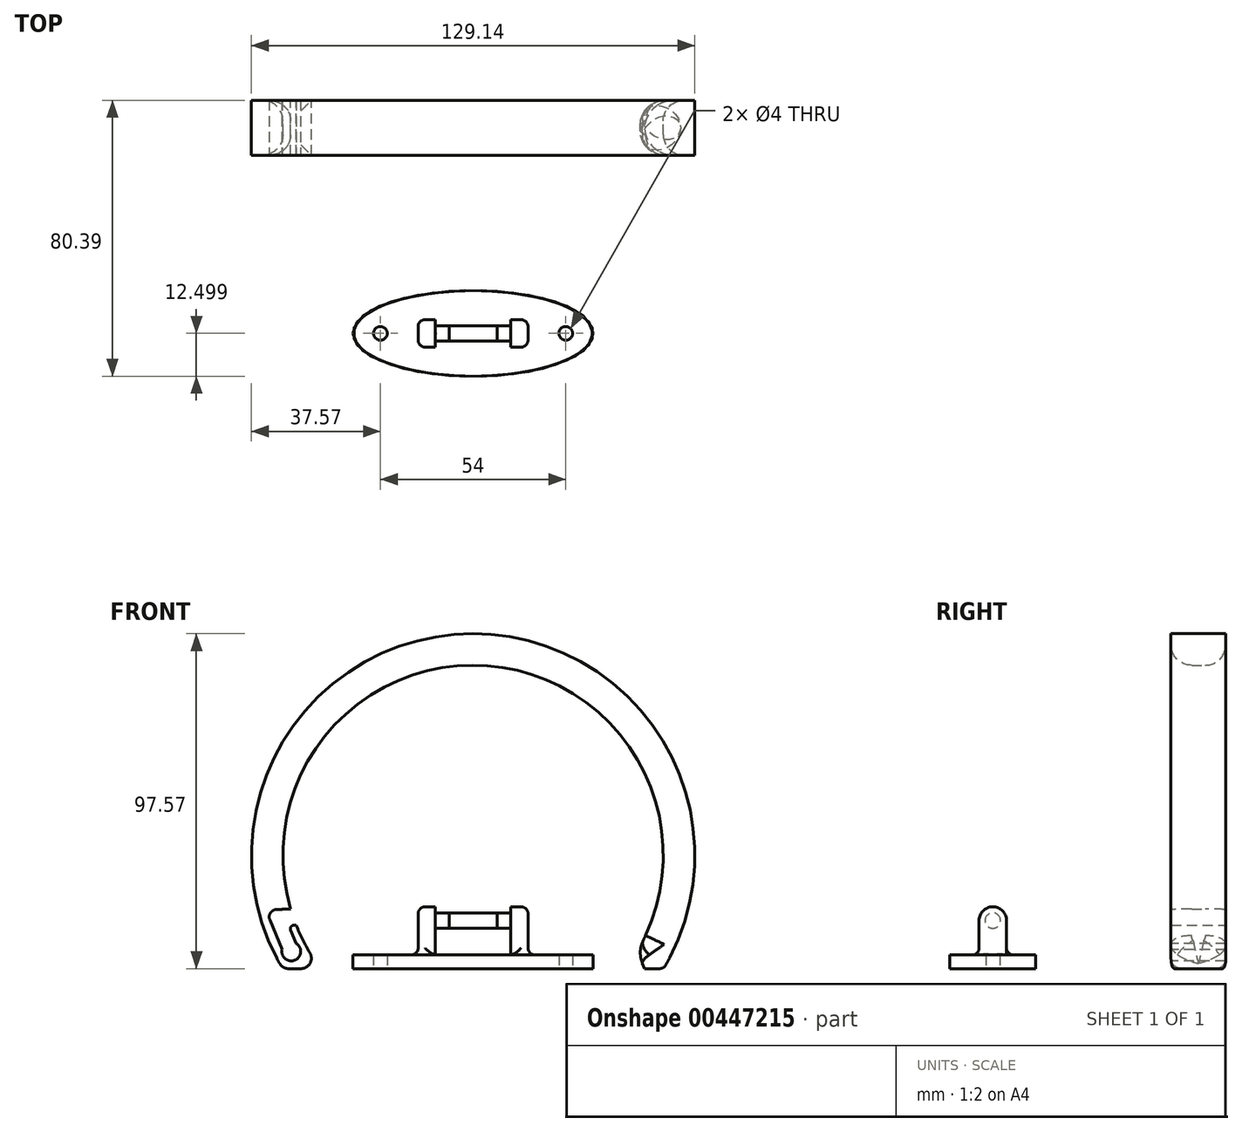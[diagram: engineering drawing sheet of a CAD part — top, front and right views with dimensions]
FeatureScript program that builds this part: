
annotation { "Feature Type Name" : "Feature", "Feature Type Description" : "" }
export const myFeature = defineFeature(function(context is Context, id is Id, definition is map)
    precondition{}
    {
        {
            var Q0;
            Q0=qCreatedBy(makeId("Front.planeOp"),FACE);
            var sketch = newSketch(context, id + "F0", { "sketchPlane" : qUnion([Q0])});
            skArc(sketch, "E0", {"start": v(50, 0) * mm, "mid": v(0, 92.9) * mm, "end": v(-50, 0) * mm});
            skArc(sketch, "E1", {"start": v(50, 0) * mm, "mid": v(41.45, -2.98) * mm, "end": v(36.33, 4.49) * mm});
            skSolve(sketch);
        }
        {
            var Q0;
            Q0=qCreatedBy(makeId("Top.planeOp"),FACE);
            var sketch = newSketch(context, id + "F1", { "sketchPlane" : qUnion([Q0])});
            skLineSegment(sketch, "E2.bottom", {"start": v(-44.5, 8) * mm, "end": v(-55.5, 8) * mm});
            skLineSegment(sketch, "E2.top", {"start": v(-44.5, -8) * mm, "end": v(-55.5, -8) * mm});
            skLineSegment(sketch, "E2.left", {"start": v(-44.5, 8) * mm, "end": v(-44.5, -8) * mm});
            skLineSegment(sketch, "E2.right", {"start": v(-55.5, 8) * mm, "end": v(-55.5, -8) * mm});
            skPoint(sketch, "E2.middle", {"position": v(-50, 0) * mm});
            skSolve(sketch);
        }
        {
            var Q0;
            Q0=makeQuery(id+"F1.imprint","IMPRINT",FACE,{"disambiguationData":[TD([[makeQuery(id+"F1.imprint","IMPRINT",EDGE,{"derivedFrom":sQuery(id+"F1.wireOp",EDGE,"E2.bottom")}),1.0]])]});
            var Q1;
            Q1=sQuery(id+"F0.wireOp",EDGE,"E0");
            sweep(context, id + "F2", {"profiles" : qUnion([Q0]), "path" : qUnion([Q1])});
        }
        {
            var Q0;
            Q0=makeQuery(id+"F2.opSweep","CAP_EDGE",EDGE,{"disambiguationData":[OSD([sQuery(id+"F0.wireOp",VERTEX,"E0.end"),sQuery(id+"F1.wireOp",EDGE,"ZPRCqQeq-nia5-ead6-5WME-yqNuvtyTv4r0")])],"isStart":true});
            fillet(context, id + "F3", {"entities" : qUnion([Q0]), "radius" : 3 * mm, "tangentPropagation" : true, "allowEdgeOverflow" : false});
        }
        {
            var Q0;
            Q0=qCreatedBy(makeId("Front.planeOp"),FACE);
            var sketch = newSketch(context, id + "F4", { "sketchPlane" : qUnion([Q0])});
            skPoint(sketch, "E3", {"position": v(-52.96, 5) * mm});
            skPoint(sketch, "E4", {"position": v(-57.14, 15) * mm});
            skPoint(sketch, "E5", {"position": v(-47.14, 15) * mm});
            skCircle(sketch, "E6", {"center": v(-47.14, 15) * mm, "radius": 2.5 * mm});
            skCircle(sketch, "E7", {"center": v(-57.14, 15) * mm, "radius": 2.25 * mm});
            skCircle(sketch, "E8", {"center": v(-52.96, 5) * mm, "radius": 2.25 * mm});
            skLineSegment(sketch, "E9", {"start": v(-50.89, 5.87) * mm, "end": v(-55.06, 15.87) * mm});
            skLineSegment(sketch, "E10", {"start": v(-55.04, 4.13) * mm, "end": v(-59.22, 14.13) * mm});
            skLineSegment(sketch, "E11", {"start": v(-47.2, 17.5) * mm, "end": v(-57.2, 17.25) * mm});
            skLineSegment(sketch, "E12", {"start": v(-47.2, 12.5) * mm, "end": v(-57.2, 12.75) * mm});
            skCircle(sketch, "E13", {"center": v(-52.96, 5) * mm, "radius": 2.75 * mm});
            skSolve(sketch);
        }
        {
            var Q0;
            {var subQ0=sQuery(id+"F4.wireOp",EDGE,"E6");var subQ1=makeQuery(id+"F4.imprint","INTERSECT",VERTEX,{"derivedFrom":[subQ0,sQuery(id+"F4.wireOp",EDGE,"E11")]});Q0=makeQuery(id+"F4.imprint","IMPRINT",FACE,{"disambiguationData":[TD([[makeQuery(id+"F4.imprint","IMPRINT",EDGE,{"disambiguationData":[TD([[subQ1,-1.0]])],"derivedFrom":subQ0}),1.0]])]});}
            var Q1;
            {var subQ0=sQuery(id+"F4.wireOp",EDGE,"E11");Q1=makeQuery(id+"F4.imprint","IMPRINT",FACE,{"disambiguationData":[TD([[makeQuery(id+"F4.imprint","IMPRINT",EDGE,{"derivedFrom":subQ0}),1.0]])]});}
            var Q2;
            {var subQ0=sQuery(id+"F4.wireOp",EDGE,"E7");var subQ1=makeQuery(id+"F4.imprint","INTERSECT",VERTEX,{"derivedFrom":[subQ0,sQuery(id+"F4.wireOp",EDGE,"E9")]});Q2=makeQuery(id+"F4.imprint","IMPRINT",FACE,{"disambiguationData":[TD([[makeQuery(id+"F4.imprint","IMPRINT",EDGE,{"disambiguationData":[TD([[subQ1,-1.0]])],"derivedFrom":subQ0}),1.0]])]});}
            var Q3;
            {var subQ1=sQuery(id+"F4.wireOp",EDGE,"E7");var subQ5=sQuery(id+"F4.wireOp",EDGE,"E10");var subQ6=makeQuery(id+"F4.imprint","INTERSECT",VERTEX,{"derivedFrom":[subQ1,subQ5]});Q3=makeQuery(id+"F4.imprint","IMPRINT",FACE,{"disambiguationData":[TD([[makeQuery(id+"F4.imprint","IMPRINT",EDGE,{"disambiguationData":[TD([[subQ6,-1.0]])],"derivedFrom":subQ1}),-1.0]])]});}
            var Q4;
            {var subQ0=sQuery(id+"F4.wireOp",EDGE,"E9");var subQ1=sQuery(id+"F4.wireOp",EDGE,"E7");var subQ2=makeQuery(id+"F4.imprint","INTERSECT",VERTEX,{"derivedFrom":[subQ1,subQ0]});Q4=makeQuery(id+"F4.imprint","IMPRINT",FACE,{"disambiguationData":[TD([[makeQuery(id+"F4.imprint","IMPRINT",EDGE,{"disambiguationData":[TD([[subQ2,1.0]])],"derivedFrom":subQ1}),-1.0]])]});}
            var Q5;
            {var subQ0=sQuery(id+"F4.wireOp",EDGE,"E9");var subQ1=sQuery(id+"F4.wireOp",EDGE,"E8");var subQ2=makeQuery(id+"F4.imprint","INTERSECT",VERTEX,{"derivedFrom":[subQ1,subQ0]});Q5=makeQuery(id+"F4.imprint","IMPRINT",FACE,{"disambiguationData":[TD([[makeQuery(id+"F4.imprint","IMPRINT",EDGE,{"disambiguationData":[TD([[subQ2,-1.0]])],"derivedFrom":subQ1}),-1.0]])]});}
            var Q6;
            {var subQ0=sQuery(id+"F4.wireOp",EDGE,"E9");var subQ1=sQuery(id+"F4.wireOp",EDGE,"E8");var subQ2=makeQuery(id+"F4.imprint","INTERSECT",VERTEX,{"derivedFrom":[subQ1,subQ0]});Q6=makeQuery(id+"F4.imprint","IMPRINT",FACE,{"disambiguationData":[TD([[makeQuery(id+"F4.imprint","IMPRINT",EDGE,{"disambiguationData":[TD([[subQ2,1.0]])],"derivedFrom":subQ1}),-1.0]])]});}
            var Q7;
            {var subQ0=sQuery(id+"F4.wireOp",EDGE,"E8");var subQ1=makeQuery(id+"F4.imprint","INTERSECT",VERTEX,{"derivedFrom":[subQ0,sQuery(id+"F4.wireOp",EDGE,"E9")]});Q7=makeQuery(id+"F4.imprint","IMPRINT",FACE,{"disambiguationData":[TD([[makeQuery(id+"F4.imprint","IMPRINT",EDGE,{"disambiguationData":[TD([[subQ1,-1.0]])],"derivedFrom":subQ0}),1.0]])]});}
            extrude(context, id + "F5", {"entities" : qUnion([Q0, Q1, Q2, Q3, Q4, Q5, Q6, Q7]), "operationType" : NewBodyOperationType.REMOVE, "oppositeDirection" : true, "depth" : 12 * mm, "hasSecondDirection" : true, "secondDirectionOppositeDirection" : false, "secondDirectionDepth" : 12 * mm, "offsetDistance" : 25 * mm});
        }
        {
            var Q0;
            Q0=makeQuery(id+"F5.boolean.opBoolean","COPY",EDGE,{"derivedFrom":makeQuery(id+"F5.opExtrude","SWEPT_EDGE",EDGE,{"disambiguationData":[OSD([sQuery(id+"F4.wireOp",EDGE,"E9"),sQuery(id+"F4.wireOp",EDGE,"E12")])]})});
            fillet(context, id + "F6", {"entities" : qUnion([Q0]), "radius" : 1 * mm, "tangentPropagation" : true, "allowEdgeOverflow" : false});
        }
        {
            var Q0;
            {var subQ0=sQuery(id+"F1.wireOp",EDGE,"E2.left");var subQ1=sQuery(id+"F1.wireOp",EDGE,"E2.bottom");var subQ2=sQuery(id+"F0.wireOp",EDGE,"E0");Q0=makeQuery(id+"F5.boolean.opBoolean","SPLIT",EDGE,{"disambiguationData":[TD([makeQuery(id+"F5.opExtrude","SWEPT_FACE",FACE,{"disambiguationData":[OSD([sQuery(id+"F4.wireOp",EDGE,"E11")])]})])],"derivedFrom":makeQuery(id+"F2.opSweep","SWEPT_EDGE",EDGE,{"disambiguationData":[OSD([subQ2,subQ1,subQ0])]})});}
            var Q1;
            {var subQ0=sQuery(id+"F1.wireOp",EDGE,"E2.left");var subQ1=sQuery(id+"F1.wireOp",EDGE,"E2.top");var subQ2=sQuery(id+"F0.wireOp",EDGE,"E0");Q1=makeQuery(id+"F5.boolean.opBoolean","SPLIT",EDGE,{"disambiguationData":[TD([makeQuery(id+"F5.opExtrude","SWEPT_FACE",FACE,{"disambiguationData":[OSD([sQuery(id+"F4.wireOp",EDGE,"E11")])]})])],"derivedFrom":makeQuery(id+"F2.opSweep","SWEPT_EDGE",EDGE,{"disambiguationData":[OSD([subQ2,subQ1,subQ0])]})});}
            fillet(context, id + "F7", {"entities" : qUnion([Q0, Q1]), "radius" : 6 * mm, "tangentPropagation" : true, "allowEdgeOverflow" : false});
        }
        {
            var Q0;
            Q0=makeQuery(id+"F2.opSweep","CAP_EDGE",EDGE,{"disambiguationData":[OSD([sQuery(id+"F0.wireOp",VERTEX,"E0.start"),sQuery(id+"F1.wireOp",EDGE,"E2.left")])],"isStart":false});
            fillet(context, id + "F8", {"entities" : qUnion([Q0]), "radius" : 8 * mm, "tangentPropagation" : true, "allowEdgeOverflow" : false});
        }
        {
            var Q0;
            Q0=qCreatedBy(makeId("Top.planeOp"),FACE);
            var sketch = newSketch(context, id + "F9", { "sketchPlane" : qUnion([Q0])});
            skLineSegment(sketch, "E14.bottom", {"start": v(68.74, 41) * mm, "end": v(27.5, 41) * mm});
            skLineSegment(sketch, "E14.top", {"start": v(68.74, -30.42) * mm, "end": v(27.5, -30.42) * mm});
            skLineSegment(sketch, "E14.left", {"start": v(68.74, 41) * mm, "end": v(68.74, -30.42) * mm});
            skLineSegment(sketch, "E14.right", {"start": v(27.5, 41) * mm, "end": v(27.5, -30.42) * mm});
            skSolve(sketch);
        }
        {
            var Q0;
            Q0=makeQuery(id+"F9.imprint","IMPRINT",FACE,{"disambiguationData":[TD([[makeQuery(id+"F9.imprint","IMPRINT",EDGE,{"derivedFrom":sQuery(id+"F9.wireOp",EDGE,"E14.bottom")}),1.0]])]});
            extrude(context, id + "F10", {"entities" : qUnion([Q0]), "operationType" : NewBodyOperationType.REMOVE, "oppositeDirection" : true, "depth" : 25 * mm});
        }
        {
            var Q0;
            Q0=makeQuery(id+"F10.boolean.opBoolean","INTERSECT",EDGE,{"derivedFrom":[makeQuery(id+"F2.opSweep","SWEPT_FACE",FACE,{"disambiguationData":[OSD([sQuery(id+"F0.wireOp",EDGE,"E0"),sQuery(id+"F1.wireOp",EDGE,"E2.right")])]}),makeQuery(id+"F10.opExtrude","CAP_FACE",FACE,{"disambiguationData":[OSD([sQuery(id+"F9.wireOp",EDGE,"E14.bottom"),sQuery(id+"F9.wireOp",EDGE,"E14.top"),sQuery(id+"F9.wireOp",EDGE,"E14.left"),sQuery(id+"F9.wireOp",EDGE,"E14.right")])],"isStart":true})]});
            var Q1;
            Q1=makeQuery(id+"F10.boolean.opBoolean","INTERSECT",EDGE,{"derivedFrom":[makeQuery(id+"F2.opSweep","CAP_FACE",FACE,{"disambiguationData":[OSD([sQuery(id+"F0.wireOp",VERTEX,"E0.start"),sQuery(id+"F1.wireOp",EDGE,"E2.bottom"),sQuery(id+"F1.wireOp",EDGE,"E2.top"),sQuery(id+"F1.wireOp",EDGE,"E2.left"),sQuery(id+"F1.wireOp",EDGE,"E2.right")])],"isStart":false}),makeQuery(id+"F10.opExtrude","CAP_FACE",FACE,{"disambiguationData":[OSD([sQuery(id+"F9.wireOp",EDGE,"E14.bottom"),sQuery(id+"F9.wireOp",EDGE,"E14.top"),sQuery(id+"F9.wireOp",EDGE,"E14.left"),sQuery(id+"F9.wireOp",EDGE,"E14.right")])],"isStart":true})]});
            fillet(context, id + "F11", {"entities" : qUnion([Q0, Q1]), "radius" : 2 * mm, "tangentPropagation" : true, "allowEdgeOverflow" : false});
        }
        {
            var Q0;
            Q0=qCreatedBy(makeId("Top.planeOp"),FACE);
            var sketch = newSketch(context, id + "F12", { "sketchPlane" : qUnion([Q0])});
            skEllipse(sketch, "E15", {"center": v(0, -59.9) * mm, "majorRadius": 35 * mm, "minorRadius": 12.5 * mm, "majorAxis": v(1, 0)});
            skPoint(sketch, "E16", {"position": v(27, -59.9) * mm});
            skPoint(sketch, "E17", {"position": v(-27, -59.9) * mm});
            skSolve(sketch);
        }
        {
            var Q0;
            Q0=makeQuery(id+"F12.imprint","IMPRINT",FACE,{"disambiguationData":[TD([[makeQuery(id+"F12.imprint","IMPRINT",EDGE,{"derivedFrom":sQuery(id+"F12.wireOp",EDGE,"E15")}),1.0]])]});
            extrude(context, id + "F13", {"entities" : qUnion([Q0]), "depth" : 4 * mm});
        }
        {
            var Q0;
            Q0=qCreatedBy(makeId("Right.planeOp"),FACE);
            cPlane(context, id + "F14", {"entities" : qUnion([Q0]), "cplaneType" : CPlaneType.OFFSET, "offset" : 11 * mm, "width" : 150 * mm, "height" : 150 * mm});
        }
        {
            var Q0;
            Q0=qCreatedBy(id+"F14.planeOp",FACE);
            var sketch = newSketch(context, id + "F15", { "sketchPlane" : qUnion([Q0])});
            skLineSegment(sketch, "E18.bottom", {"start": v(-63.9, 0) * mm, "end": v(-55.9, 0) * mm});
            skLineSegment(sketch, "E18.top", {"start": v(-63.9, 18) * mm, "end": v(-55.9, 18) * mm});
            skLineSegment(sketch, "E18.left", {"start": v(-63.9, 0) * mm, "end": v(-63.9, 18) * mm});
            skLineSegment(sketch, "E18.right", {"start": v(-55.9, 0) * mm, "end": v(-55.9, 18) * mm});
            skCircle(sketch, "E19", {"center": v(-59.9, 14) * mm, "radius": 2.25 * mm});
            skSolve(sketch);
        }
        {
            var Q0;
            Q0=makeQuery(id+"F15.imprint","IMPRINT",FACE,{"disambiguationData":[TD([[makeQuery(id+"F15.imprint","IMPRINT",EDGE,{"derivedFrom":sQuery(id+"F15.wireOp",EDGE,"E18.bottom")}),1.0]])]});
            var Q1;
            Q1=makeQuery(id+"F15.imprint","IMPRINT",FACE,{"disambiguationData":[TD([[makeQuery(id+"F15.imprint","IMPRINT",EDGE,{"derivedFrom":sQuery(id+"F15.wireOp",EDGE,"E19")}),1.0]])]});
            extrude(context, id + "F16", {"entities" : qUnion([Q0, Q1]), "operationType" : NewBodyOperationType.ADD, "depth" : 5 * mm});
        }
        {
            var Q0;
            Q0=makeQuery(id+"F15.imprint","IMPRINT",FACE,{"disambiguationData":[TD([[makeQuery(id+"F15.imprint","IMPRINT",EDGE,{"derivedFrom":sQuery(id+"F15.wireOp",EDGE,"E19")}),1.0]])]});
            var Q1;
            Q1=sQuery(id+"F15.wireOp",EDGE,"E19");
            extrude(context, id + "F17", {"entities" : qUnion([Q0]), "operationType" : NewBodyOperationType.ADD, "surfaceEntities" : qUnion([Q1]), "oppositeDirection" : true, "depth" : 18 * mm});
        }
        {
            var Q0;
            Q0=makeQuery(id+"F16.opExtrude","SWEPT_EDGE",EDGE,{"disambiguationData":[OSD([sQuery(id+"F15.wireOp",EDGE,"E18.top"),sQuery(id+"F15.wireOp",EDGE,"E18.left")])]});
            var Q1;
            Q1=makeQuery(id+"F16.opExtrude","SWEPT_EDGE",EDGE,{"disambiguationData":[OSD([sQuery(id+"F15.wireOp",EDGE,"E18.top"),sQuery(id+"F15.wireOp",EDGE,"E18.right")])]});
            fillet(context, id + "F18", {"entities" : qUnion([Q0, Q1]), "radius" : 4 * mm, "tangentPropagation" : true, "allowEdgeOverflow" : false});
        }
        {
            var Q0;
            Q0=makeQuery(id+"F16.opExtrude","CAP_FACE",FACE,{"disambiguationData":[OSD([sQuery(id+"F15.wireOp",EDGE,"E18.bottom"),sQuery(id+"F15.wireOp",EDGE,"E18.top"),sQuery(id+"F15.wireOp",EDGE,"E18.left"),sQuery(id+"F15.wireOp",EDGE,"E18.right")])],"isStart":false});
            fillet(context, id + "F19", {"entities" : qUnion([Q0]), "radius" : 2 * mm, "tangentPropagation" : true, "allowEdgeOverflow" : false});
        }
        {
            var Q0;
            Q0=makeQuery(id+"F13.opExtrude","SWEPT_BODY",BODY,{"disambiguationData":[OSD([sQuery(id+"F12.wireOp",EDGE,"E15")])]});
            var Q1;
            Q1=qCreatedBy(makeId("Right.planeOp"),FACE);
            mirror(context, id + "F20", {"operationType" : NewBodyOperationType.ADD, "entities" : qUnion([Q0]), "mirrorPlane" : qUnion([Q1])});
        }
        {
            var Q0;
            Q0=sQuery(id+"F12.wireOp",VERTEX,"E16");
            var Q1;
            Q1=sQuery(id+"F12.wireOp",VERTEX,"E17");
            var Q2;
            Q2=makeQuery(id+"F13.opExtrude","SWEPT_BODY",BODY,{"disambiguationData":[OSD([sQuery(id+"F12.wireOp",EDGE,"E15")])]});
            hole(context, id + "F21", {"style" : HoleStyle.SIMPLE, "endStyle" : HoleEndStyle.THROUGH, "oppositeDirection" : true, "holeDiameter" : 4 * mm, "isTappedThrough" : true, "tappedDepth" : 12 * mm, "tapClearance" : 3, "locations" : qUnion([Q0, Q1]), "scope" : qUnion([Q2])});
        }
    });
